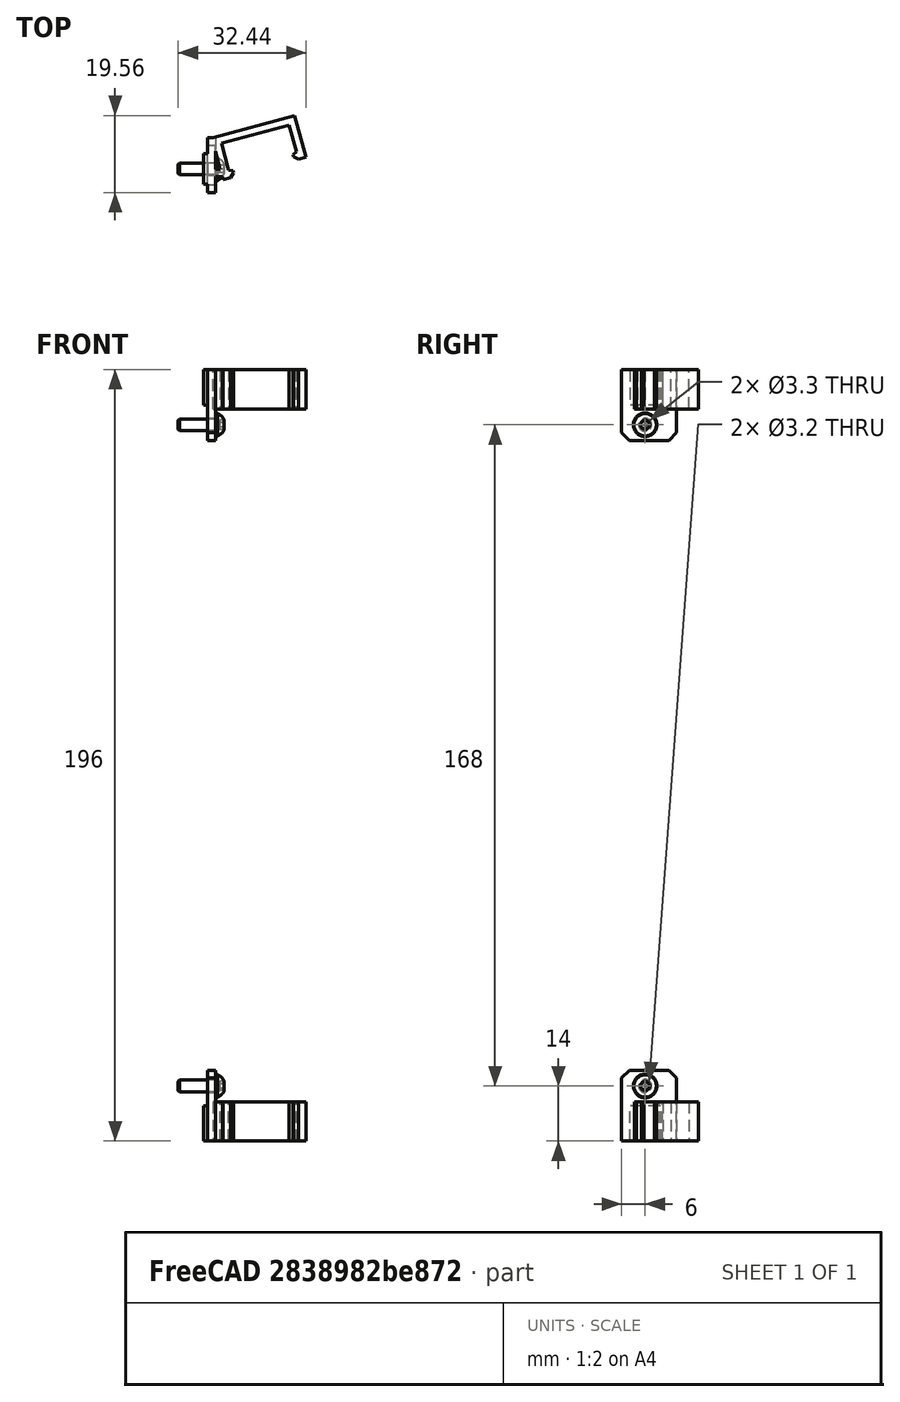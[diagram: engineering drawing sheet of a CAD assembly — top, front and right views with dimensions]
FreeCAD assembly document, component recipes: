
FREECAD ASSEMBLY — COMPONENT RECIPES ("neo-pixel-assembly")

This assembly document has 2 components, labeled P0..P1 below (a component is one placed body or linked part). 1 of them carries a construction recipe — the FreeCAD feature program that regenerates the part from scratch, quoted from this document or its linked companion documents; the rest are supplied as boundary geometry only. No exploded tour is included for this assembly.
COMPONENT P0 — geometry summary ("neo-pixel-mount"; no construction recipe available for this part):
  bounding box: 196.0 x 32.4 x 19.6 mm
  tessellated surface: 660 triangles
  volume: 1393334313771970003795799310896004173226586922408213830850045488612256453752126949198291730019716694016 mm^3 (1120440788053146064594466655154030762944774090875112219224454086863764007370477546307570627350888448% of its bounding box)
  symmetry: mirror-symmetric across its z mid-plane
COMPONENT P1 — recipe-attached ("right-panel", a linked part whose construction recipe lives in a companion FreeCAD document of the same project; that document's serialized recipe follows).
Construction recipe (the companion document, serialized — sketch geometry with constraints, then the solid features built on it; lengths are millimeters unless a unit is written):

FCSTD DOCUMENT  (FreeCAD 0.19R24291 (Git))
Label: right-panel-assembly
License: All rights reserved
LicenseURL: http://en.wikipedia.org/wiki/All_rights_reserved
objects: Part::Feature×24, App::Part×13, Part::FeaturePython×12, PartDesign::CoordinateSystem×1, Part::Box×1
note: 38 computed .brp shape members not serialized (recipe doc carries the construction recipe); baked Part::Feature solids carry a one-line shape summary decoded from their .brp

FEATURE [Part::Feature] Chamfer008001013  label="mounter-inner"
  shape: bbox 28 x 22 x 6 mm, 82 faces (baked)
FEATURE [Part::FeaturePython] Screw055  label="M6x16-Screw001"  # Fasteners workbench fastener (typed FeaturePython)
  Placement = pos=(15,0,7) rot=(0,0,1;0rad)
  baseObject = -> Chamfer008002001003 [Edge135]
  diameter = 4
  invert = false
  length = 3
  lengthCustom = 16
  matchOuter = false
  offset = 0
  thread = false
  type = 40
FEATURE [Part::Feature] Chamfer008002001009  label="mounter-inner004"
  shape: bbox 28 x 22 x 6 mm, 82 faces (baked)
FEATURE [Part::Feature] Chamfer008002001002  label="mounter-inner001"
  shape: bbox 28 x 22 x 6 mm, 82 faces (baked)
FEATURE [Part::Feature] Chamfer008002001004  label="mounter-inner002"
  shape: bbox 28 x 22 x 6 mm, 82 faces (baked)
FEATURE [Part::Feature] Chamfer008002001007  label="mounter-outer008"
  shape: bbox 17 x 28 x 11 mm, 53 faces (baked)
FEATURE [Part::Feature] Chamfer008002001016  label="mounter-inner008"
  shape: bbox 28 x 22 x 6 mm, 82 faces (baked)
FEATURE [Part::FeaturePython] Screw063  label="M6x16-Screw013"  # Fasteners workbench fastener (typed FeaturePython)
  Placement = pos=(15,0,7) rot=(0,0,1;0rad)
  baseObject = -> Chamfer008002001019 [Edge135]
  diameter = 4
  invert = false
  length = 3
  lengthCustom = 16
  matchOuter = false
  offset = 0
  thread = false
  type = 40
FEATURE [Part::Feature] Chamfer008002001022  label="mounter-inner011"
  shape: bbox 28 x 22 x 6 mm, 82 faces (baked)
FEATURE [Part::Feature] Chamfer008002001011  label="mounter-inner005"
  shape: bbox 28 x 22 x 6 mm, 82 faces (baked)
FEATURE [Part::FeaturePython] Screw057  label="M6x16-Screw003"  # Fasteners workbench fastener (typed FeaturePython)
  Placement = pos=(15,0,7) rot=(0,0,1;0rad)
  baseObject = -> Chamfer008002001007 [Edge135]
  diameter = 4
  invert = false
  length = 3
  lengthCustom = 16
  matchOuter = false
  offset = 0
  thread = false
  type = 40
FEATURE [Part::FeaturePython] Screw054  label="M6x16-Screw007"  # Fasteners workbench fastener (typed FeaturePython)
  Placement = pos=(15,0,7) rot=(0,0,1;0rad)
  baseObject = -> Chamfer008002001001 [Edge135]
  diameter = 4
  invert = false
  length = 3
  lengthCustom = 16
  matchOuter = false
  offset = 0
  thread = false
  type = 40
FEATURE [Part::Feature] Chamfer008002001012  label="mounter-outer005"
  shape: bbox 17 x 28 x 11 mm, 53 faces (baked)
FEATURE [Part::FeaturePython] Screw056  label="M6x16-Screw002"  # Fasteners workbench fastener (typed FeaturePython)
  Placement = pos=(15,0,7) rot=(0,0,1;0rad)
  baseObject = -> Chamfer008002001005 [Edge135]
  diameter = 4
  invert = false
  length = 3
  lengthCustom = 16
  matchOuter = false
  offset = 0
  thread = false
  type = 40
FEATURE [Part::Feature] Chamfer008002001020  label="mounter-outer001"
  shape: bbox 17 x 28 x 11 mm, 53 faces (baked)
FEATURE [Part::Feature] Chamfer008002001003  label="mounter-outer010"
  shape: bbox 17 x 28 x 11 mm, 53 faces (baked)
FEATURE [Part::FeaturePython] Screw062  label="M6x16-Screw012"  # Fasteners workbench fastener (typed FeaturePython)
  Placement = pos=(15,0,7) rot=(0,0,1;0rad)
  baseObject = -> Chamfer008002001017 [Edge135]
  diameter = 4
  invert = false
  length = 3
  lengthCustom = 16
  matchOuter = false
  offset = 0
  thread = false
  type = 40
FEATURE [Part::FeaturePython] Screw060  label="M6x16-Screw010"  # Fasteners workbench fastener (typed FeaturePython)
  Placement = pos=(15,0,7) rot=(0,0,1;0rad)
  baseObject = -> Chamfer008002001012 [Edge135]
  diameter = 4
  invert = false
  length = 3
  lengthCustom = 16
  matchOuter = false
  offset = 0
  thread = false
  type = 40
FEATURE [Part::Feature] Chamfer008002001013  label="mounter-inner006"
  shape: bbox 28 x 22 x 6 mm, 82 faces (baked)
FEATURE [Part::Feature] Chamfer008002001019  label="mounter-outer002"
  shape: bbox 17 x 28 x 11 mm, 53 faces (baked)
FEATURE [Part::Feature] Chamfer008002001006  label="mounter-inner003"
  shape: bbox 28 x 22 x 6 mm, 82 faces (baked)
FEATURE [App::Part] Part016  label="Panel-mounterr2-003"
  Group = -> [Chamfer008002001006,Chamfer008002001007,Screw057]
  Origin = -> Origin016
  Placement = pos=(315,3,39) rot=(-1,0,0;4.71239rad)
FEATURE [Part::FeaturePython] Screw064  label="M6x16-Screw014"  # Fasteners workbench fastener (typed FeaturePython)
  Placement = pos=(15,0,7) rot=(0,0,1;0rad)
  baseObject = -> Chamfer008002001020 [Edge135]
  diameter = 4
  invert = false
  length = 3
  lengthCustom = 16
  matchOuter = false
  offset = 0
  thread = false
  type = 40
FEATURE [PartDesign::CoordinateSystem] LCS_right_panel  label="LCS_right-panel"
  AttacherType = Attacher::AttachEngine3D
FEATURE [Part::Feature] Chamfer008002001023  label="mounter-outer"
  shape: bbox 17 x 28 x 11 mm, 53 faces (baked)
FEATURE [Part::Feature] Chamfer008002001018  label="mounter-inner009"
  shape: bbox 28 x 22 x 6 mm, 82 faces (baked)
FEATURE [App::Part] Part022  label="Panel-mounterr2-009"
  Group = -> [Chamfer008002001018,Chamfer008002001019,Screw063]
  Origin = -> Origin022
  Placement = pos=(39,3,445) rot=(-0.57735,0.57735,-0.57735;4.18879rad)
FEATURE [Part::Feature] Chamfer008002001001  label="mounter-outer011"
  shape: bbox 17 x 28 x 11 mm, 53 faces (baked)
FEATURE [App::Part] Part013  label="Panel-mounterr2-000"
  Group = -> [Chamfer008001013,Chamfer008002001001,Screw054]
  Origin = -> Origin013
  Placement = pos=(39,3,5) rot=(-0.57735,-0.57735,0.57735;4.18879rad)
FEATURE [Part::Feature] Chamfer008002001014  label="mounter-inner007"
  shape: bbox 28 x 22 x 6 mm, 82 faces (baked)
FEATURE [Part::Feature] Chamfer008002001008  label="mounter-outer007"
  shape: bbox 17 x 28 x 11 mm, 53 faces (baked)
FEATURE [Part::Feature] Chamfer008002001017  label="mounter-outer003"
  shape: bbox 17 x 28 x 11 mm, 53 faces (baked)
FEATURE [App::Part] Part021  label="Panel-mounterr2-008"
  Group = -> [Chamfer008002001016,Chamfer008002001017,Screw062]
  Origin = -> Origin021
  Placement = pos=(5,3,411) rot=(0,0.707107,-0.707107;3.14159rad)
FEATURE [Part::Box] Box002  label="panel-324x454x3mm"
  AttacherType = Attacher::AttachEngine3D
  Height = 454
  Length = 324
  Placement = pos=(-2,0,-2) rot=(0,0,1;0rad)
  Width = 3
FEATURE [Part::Feature] Chamfer008002001015  label="mounter-outer004"
  shape: bbox 17 x 28 x 11 mm, 53 faces (baked)
FEATURE [Part::Feature] Chamfer008002001010  label="mounter-outer006"
  shape: bbox 17 x 28 x 11 mm, 53 faces (baked)
FEATURE [App::Part] Part019  label="Panel-mounterr2-006"
  Group = -> [Chamfer008002001013,Chamfer008002001012,Screw060]
  Origin = -> Origin019
  Placement = pos=(281,3,445) rot=(-0.57735,0.57735,-0.57735;4.18879rad)
FEATURE [Part::FeaturePython] Screw065  label="M6x16-Screw015"  # Fasteners workbench fastener (typed FeaturePython)
  Placement = pos=(15,0,7) rot=(0,0,1;0rad)
  baseObject = -> Chamfer008002001023 [Edge135]
  diameter = 4
  invert = false
  length = 3
  lengthCustom = 16
  matchOuter = false
  offset = 0
  thread = false
  type = 40
FEATURE [Part::FeaturePython] Screw061  label="M6x16-Screw011"  # Fasteners workbench fastener (typed FeaturePython)
  Placement = pos=(15,0,7) rot=(0,0,1;0rad)
  baseObject = -> Chamfer008002001015 [Edge135]
  diameter = 4
  invert = false
  length = 3
  lengthCustom = 16
  matchOuter = false
  offset = 0
  thread = false
  type = 40
FEATURE [App::Part] Part020  label="Panel-mounterr2-007"
  Group = -> [Chamfer008002001014,Chamfer008002001015,Screw061]
  Origin = -> Origin020
  Placement = pos=(160,3,445) rot=(-0.57735,0.57735,-0.57735;4.18879rad)
FEATURE [Part::FeaturePython] Screw058  label="M6x16-Screw008"  # Fasteners workbench fastener (typed FeaturePython)
  Placement = pos=(15,0,7) rot=(0,0,1;0rad)
  baseObject = -> Chamfer008002001008 [Edge135]
  diameter = 4
  invert = false
  length = 3
  lengthCustom = 16
  matchOuter = false
  offset = 0
  thread = false
  type = 40
FEATURE [App::Part] Part017  label="Panel-mounterr2-004"
  Group = -> [Chamfer008002001009,Chamfer008002001008,Screw058]
  Origin = -> Origin017
  Placement = pos=(315,3,215) rot=(-1,0,0;4.71239rad)
FEATURE [App::Part] Part024  label="Panel-mounterr2-011"
  Group = -> [Chamfer008002001022,Chamfer008002001023,Screw065]
  Origin = -> Origin024
  Placement = pos=(5,3,39) rot=(0,0.707107,-0.707107;3.14159rad)
FEATURE [Part::Feature] Chamfer008002001005  label="mounter-outer009"
  shape: bbox 17 x 28 x 11 mm, 53 faces (baked)
FEATURE [App::Part] Part015  label="Panel-mounterr2-002"
  Group = -> [Chamfer008002001004,Chamfer008002001005,Screw056]
  Origin = -> Origin015
  Placement = pos=(280.5,3,5) rot=(-0.57735,-0.57735,0.57735;4.18879rad)
FEATURE [Part::Feature] Chamfer008002001021  label="mounter-inner010"
  shape: bbox 28 x 22 x 6 mm, 82 faces (baked)
FEATURE [App::Part] Part023  label="Panel-mounterr2-010"
  Group = -> [Chamfer008002001021,Chamfer008002001020,Screw064]
  Origin = -> Origin023
  Placement = pos=(5,3,215) rot=(0,0.707107,-0.707107;3.14159rad)
FEATURE [Part::FeaturePython] Screw059  label="M6x16-Screw009"  # Fasteners workbench fastener (typed FeaturePython)
  Placement = pos=(15,0,7) rot=(0,0,1;0rad)
  baseObject = -> Chamfer008002001010 [Edge135]
  diameter = 4
  invert = false
  length = 3
  lengthCustom = 16
  matchOuter = false
  offset = 0
  thread = false
  type = 40
FEATURE [App::Part] Part018  label="Panel-mounterr2-005"
  Group = -> [Chamfer008002001011,Chamfer008002001010,Screw059]
  Origin = -> Origin018
  Placement = pos=(315,3,411) rot=(-1,0,0;4.71239rad)
FEATURE [App::Part] Part014  label="Panel-mounterr2-001"
  Group = -> [Chamfer008002001002,Chamfer008002001003,Screw055]
  Origin = -> Origin014
  Placement = pos=(160,3,5) rot=(-0.57735,-0.57735,0.57735;4.18879rad)
FEATURE [App::Part] Part005  label="right-panel"
  Group = -> [Box002,Part013,Part014,Part015,Part016,Part017,Part018,Part019,Part020,Part021,Part022,Part023,Part024,LCS_right_panel]
  Origin = -> Origin005
PROVENANCE & LICENSES
A FreeCAD (.FCStd) document from a public repository crawl; recipes are the document's own serialized feature recipes (and, for linked parts, companion documents' recipes).
License: gpl-3.0.
